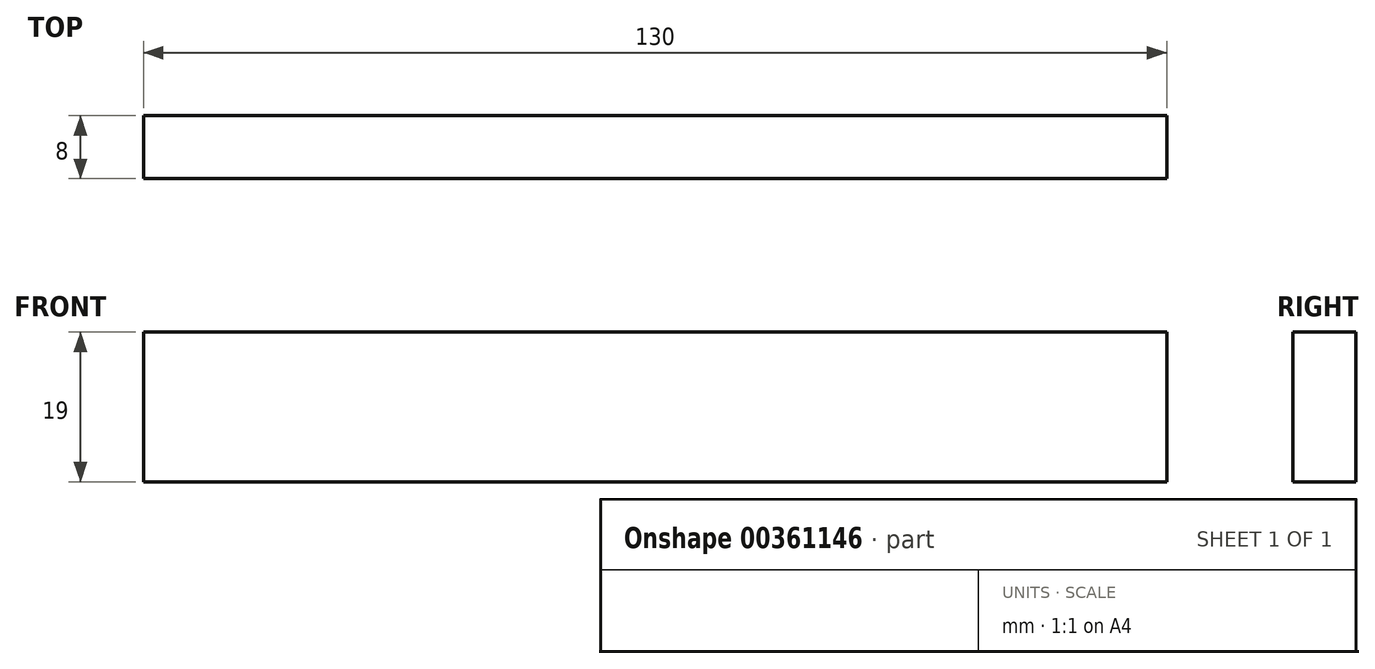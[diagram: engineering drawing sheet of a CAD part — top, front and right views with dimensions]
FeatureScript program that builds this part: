
annotation { "Feature Type Name" : "Feature", "Feature Type Description" : "" }
export const myFeature = defineFeature(function(context is Context, id is Id, definition is map)
    precondition{}
    {
        {
            var Q0;
            Q0=qCreatedBy(makeId("Front.planeOp"),FACE);
            var sketch = newSketch(context, id + "F0", { "sketchPlane" : qUnion([Q0])});
            skLineSegment(sketch, "E0.bottom", {"start": v(-65, 9.5) * mm, "end": v(65, 9.5) * mm});
            skLineSegment(sketch, "E0.top", {"start": v(-65, -9.5) * mm, "end": v(65, -9.5) * mm});
            skLineSegment(sketch, "E0.left", {"start": v(-65, 9.5) * mm, "end": v(-65, -9.5) * mm});
            skLineSegment(sketch, "E0.right", {"start": v(65, 9.5) * mm, "end": v(65, -9.5) * mm});
            skSolve(sketch);
        }
        {
            var Q0;
            Q0=makeQuery(id+"F0.imprint","IMPRINT",FACE,{"disambiguationData":[TD([[makeQuery(id+"F0.imprint","IMPRINT",EDGE,{"derivedFrom":sQuery(id+"F0.wireOp",EDGE,"E0.bottom")}),-1.0]])]});
            extrude(context, id + "F1", {"entities" : qUnion([Q0]), "depth" : 8 * mm});
        }
    });
